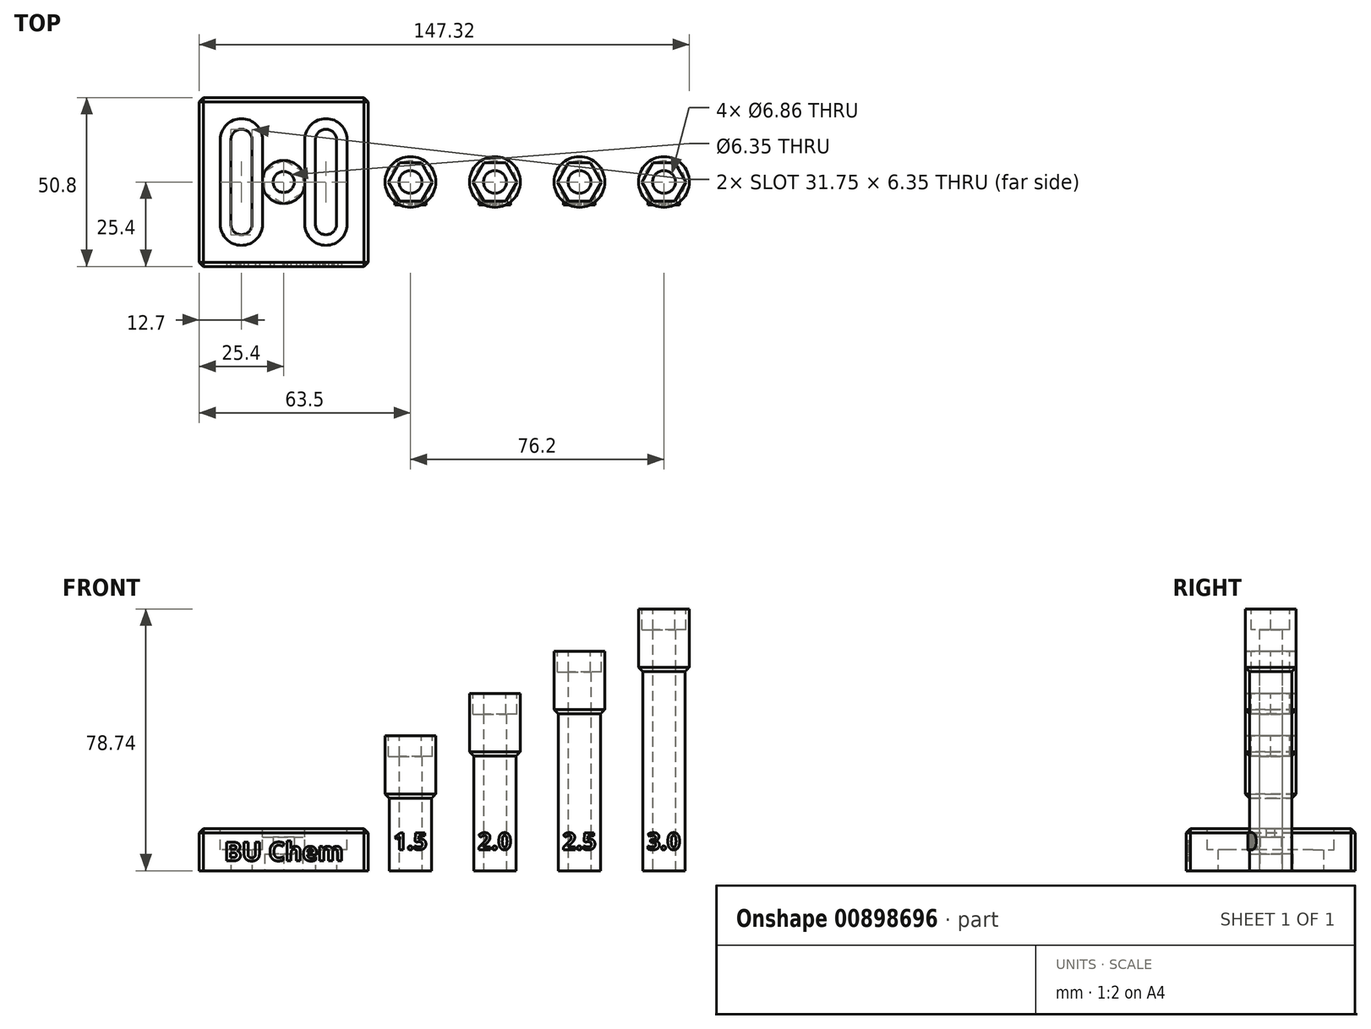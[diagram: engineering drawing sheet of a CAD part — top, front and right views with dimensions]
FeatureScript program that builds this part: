
annotation { "Feature Type Name" : "Feature", "Feature Type Description" : "" }
export const myFeature = defineFeature(function(context is Context, id is Id, definition is map)
    precondition{}
    {
        {
            var Q0;
            Q0=qCreatedBy(makeId("Top.planeOp"),FACE);
            var sketch = newSketch(context, id + "F0", { "sketchPlane" : qUnion([Q0])});
            skLineSegment(sketch, "E0.bottom", {"start": v(-25.4, 25.4) * mm, "end": v(25.4, 25.4) * mm});
            skLineSegment(sketch, "E0.top", {"start": v(-25.4, -25.4) * mm, "end": v(25.4, -25.4) * mm});
            skLineSegment(sketch, "E0.left", {"start": v(-25.4, 25.4) * mm, "end": v(-25.4, -25.4) * mm});
            skLineSegment(sketch, "E0.right", {"start": v(25.4, 25.4) * mm, "end": v(25.4, -25.4) * mm});
            skLineSegment(sketch, "E1", {"start": v(-25.4, 0) * mm, "end": v(129.63, 0) * mm, "construction": true});
            skLineSegment(sketch, "E2", {"start": v(0, -25.4) * mm, "end": v(0, 25.4) * mm, "construction": true});
            skPoint(sketch, "E3", {"position": v(0, 0) * mm});
            skCircle(sketch, "E4", {"center": v(0, 0) * mm, "radius": 3.18 * mm});
            skLineSegment(sketch, "E5", {"start": v(-25.4, -12.7) * mm, "end": v(25.4, -12.7) * mm, "construction": true});
            skLineSegment(sketch, "E6", {"start": v(-12.7, 25.4) * mm, "end": v(-12.7, -25.4) * mm, "construction": true});
            skCircle(sketch, "E7", {"center": v(-12.7, -12.7) * mm, "radius": 3.18 * mm});
            skCircle(sketch, "E8.0.1.0", {"center": v(-12.7, 12.7) * mm, "radius": 3.18 * mm});
            skCircle(sketch, "E8.1.0.0", {"center": v(12.7, -12.7) * mm, "radius": 3.18 * mm});
            skCircle(sketch, "E8.1.1.0", {"center": v(12.7, 12.7) * mm, "radius": 3.18 * mm});
            skLineSegment(sketch, "E8.direction1", {"start": v(-12.7, -12.7) * mm, "end": v(12.7, -12.7) * mm, "construction": true});
            skLineSegment(sketch, "E8.direction2", {"start": v(-12.7, -12.7) * mm, "end": v(-12.7, 12.7) * mm, "construction": true});
            skLineSegment(sketch, "E9", {"start": v(9.52, 12.7) * mm, "end": v(9.52, -12.7) * mm});
            skLineSegment(sketch, "E10", {"start": v(15.87, 12.7) * mm, "end": v(15.87, -12.7) * mm});
            skLineSegment(sketch, "E11", {"start": v(-9.53, 12.7) * mm, "end": v(-9.53, -12.7) * mm});
            skLineSegment(sketch, "E12", {"start": v(-15.88, 12.7) * mm, "end": v(-15.87, -12.7) * mm});
            skCircle(sketch, "E13.cCircle", {"center": v(0, 0) * mm, "radius": 5.72 * mm, "construction": true});
            skLineSegment(sketch, "E13.0", {"start": v(5.72, 3.3) * mm, "end": v(5.72, -3.3) * mm});
            skLineSegment(sketch, "E13.1", {"start": v(5.72, -3.3) * mm, "end": v(0, -6.6) * mm});
            skLineSegment(sketch, "E13.2", {"start": v(0, -6.6) * mm, "end": v(-5.72, -3.3) * mm});
            skLineSegment(sketch, "E13.3", {"start": v(-5.72, -3.3) * mm, "end": v(-5.72, 3.3) * mm});
            skLineSegment(sketch, "E13.4", {"start": v(-5.72, 3.3) * mm, "end": v(0, 6.6) * mm});
            skLineSegment(sketch, "E13.5", {"start": v(0, 6.6) * mm, "end": v(5.72, 3.3) * mm});
            skPoint(sketch, "E13.0.midPoint", {"position": v(5.72, 0) * mm});
            skPoint(sketch, "E14.orphan", {"position": v(25.4, 0) * mm});
            skCircle(sketch, "E15", {"center": v(38.1, 0) * mm, "radius": 6.35 * mm});
            skCircle(sketch, "E16", {"center": v(38.1, 0) * mm, "radius": 3.43 * mm});
            skCircle(sketch, "E17", {"center": v(63.5, 0) * mm, "radius": 3.43 * mm});
            skCircle(sketch, "E18", {"center": v(63.5, 0) * mm, "radius": 6.35 * mm});
            skCircle(sketch, "E19", {"center": v(88.9, 0) * mm, "radius": 3.43 * mm});
            skCircle(sketch, "E20", {"center": v(88.9, 0) * mm, "radius": 6.35 * mm});
            skCircle(sketch, "E21", {"center": v(114.3, 0) * mm, "radius": 3.43 * mm});
            skCircle(sketch, "E22", {"center": v(114.3, 0) * mm, "radius": 6.35 * mm});
            skSolve(sketch);
        }
        {
            var Q0;
            Q0=makeQuery(id+"F0.imprint","IMPRINT",FACE,{"disambiguationData":[TD([[makeQuery(id+"F0.imprint","IMPRINT",EDGE,{"derivedFrom":sQuery(id+"F0.wireOp",EDGE,"E0.bottom")}),-1.0]])]});
            var Q1;
            Q1=makeQuery(id+"F0.imprint","IMPRINT",FACE,{"disambiguationData":[TD([[makeQuery(id+"F0.imprint","IMPRINT",EDGE,{"derivedFrom":sQuery(id+"F0.wireOp",EDGE,"E4")}),-1.0]])]});
            extrude(context, id + "F1", {"entities" : qUnion([Q0, Q1]), "depth" : 12.7 * mm, "offsetDistance" : 25.4 * mm});
        }
        {
            var Q0;
            Q0=makeQuery(id+"F1.opExtrude","CAP_FACE",FACE,{"disambiguationData":[OSD([sQuery(id+"F0.wireOp",EDGE,"E0.bottom"),sQuery(id+"F0.wireOp",EDGE,"E0.top"),sQuery(id+"F0.wireOp",EDGE,"E0.left"),sQuery(id+"F0.wireOp",EDGE,"E0.right"),sQuery(id+"F0.wireOp",EDGE,"E4"),sQuery(id+"F0.wireOp",EDGE,"E7"),sQuery(id+"F0.wireOp",EDGE,"E8.0.1.0"),sQuery(id+"F0.wireOp",EDGE,"E8.1.0.0"),sQuery(id+"F0.wireOp",EDGE,"E8.1.1.0"),sQuery(id+"F0.wireOp",EDGE,"E9"),sQuery(id+"F0.wireOp",EDGE,"E10"),sQuery(id+"F0.wireOp",EDGE,"E11"),sQuery(id+"F0.wireOp",EDGE,"E12")])],"isStart":false});
            var sketch = newSketch(context, id + "F2", { "sketchPlane" : qUnion([Q0])});
            skLineSegment(sketch, "E23.0", {"start": v(-15.88, 12.7) * mm, "end": v(-15.87, -12.7) * mm, "construction": true});
            skCircle(sketch, "E24.0", {"center": v(-12.7, 12.7) * mm, "radius": 3.18 * mm, "construction": true});
            skCircle(sketch, "E25.0", {"center": v(-12.7, -12.7) * mm, "radius": 3.18 * mm, "construction": true});
            skLineSegment(sketch, "E26.0", {"start": v(-9.53, 12.7) * mm, "end": v(-9.53, -12.7) * mm, "construction": true});
            skCircle(sketch, "E27.0", {"center": v(0, 0) * mm, "radius": 3.18 * mm, "construction": true});
            skLineSegment(sketch, "E28.0", {"start": v(9.52, 12.7) * mm, "end": v(9.52, -12.7) * mm, "construction": true});
            skCircle(sketch, "E29.0", {"center": v(12.7, -12.7) * mm, "radius": 3.18 * mm, "construction": true});
            skLineSegment(sketch, "E30.0", {"start": v(15.87, 12.7) * mm, "end": v(15.87, -12.7) * mm, "construction": true});
            skCircle(sketch, "E31.0", {"center": v(12.7, 12.7) * mm, "radius": 3.18 * mm, "construction": true});
            skCircle(sketch, "E32", {"center": v(-12.7, 12.7) * mm, "radius": 6.35 * mm});
            skCircle(sketch, "E33", {"center": v(-12.7, -12.7) * mm, "radius": 6.35 * mm});
            skCircle(sketch, "E34", {"center": v(12.7, 12.7) * mm, "radius": 6.35 * mm});
            skCircle(sketch, "E35", {"center": v(12.7, -12.7) * mm, "radius": 6.35 * mm});
            skCircle(sketch, "E36", {"center": v(0, 0) * mm, "radius": 6.48 * mm});
            skLineSegment(sketch, "E37", {"start": v(-19.05, 12.7) * mm, "end": v(-19.05, -12.7) * mm});
            skLineSegment(sketch, "E38", {"start": v(-6.35, 12.7) * mm, "end": v(-6.35, -12.7) * mm});
            skLineSegment(sketch, "E39", {"start": v(6.35, 12.7) * mm, "end": v(6.35, -12.7) * mm});
            skLineSegment(sketch, "E40", {"start": v(19.05, 12.7) * mm, "end": v(19.05, -12.7) * mm});
            skSolve(sketch);
        }
        {
            var Q0;
            {var subQ0=makeQuery(id+"F1.opExtrude","CAP_EDGE",EDGE,{"disambiguationData":[OSD([sQuery(id+"F0.wireOp",EDGE,"E8.0.1.0")])],"isStart":false});Q0=makeQuery(id+"F2.imprint","IMPRINT",FACE,{"disambiguationData":[TD([[makeQuery(id+"F2.imprint","IMPRINT",EDGE,{"derivedFrom":subQ0}),-1.0]])]});}
            var Q1;
            {var subQ0=sQuery(id+"F2.wireOp",EDGE,"E37");Q1=makeQuery(id+"F2.imprint","IMPRINT",FACE,{"disambiguationData":[TD([[makeQuery(id+"F2.imprint","IMPRINT",EDGE,{"derivedFrom":subQ0}),1.0]])]});}
            var Q2;
            {var subQ0=sQuery(id+"F2.wireOp",EDGE,"E38");var subQ1=sQuery(id+"F2.wireOp",EDGE,"E32");var subQ2=makeQuery(id+"F2.imprint","INTERSECT",VERTEX,{"derivedFrom":[subQ1,subQ0]});Q2=makeQuery(id+"F2.imprint","IMPRINT",FACE,{"disambiguationData":[TD([[makeQuery(id+"F2.imprint","IMPRINT",EDGE,{"disambiguationData":[TD([[subQ2,1.0]])],"derivedFrom":subQ1}),-1.0]])]});}
            var Q3;
            {var subQ0=makeQuery(id+"F1.opExtrude","CAP_EDGE",EDGE,{"disambiguationData":[OSD([sQuery(id+"F0.wireOp",EDGE,"E7")])],"isStart":false});Q3=makeQuery(id+"F2.imprint","IMPRINT",FACE,{"disambiguationData":[TD([[makeQuery(id+"F2.imprint","IMPRINT",EDGE,{"derivedFrom":subQ0}),-1.0]])]});}
            var Q4;
            {var subQ0=makeQuery(id+"F1.opExtrude","CAP_EDGE",EDGE,{"disambiguationData":[OSD([sQuery(id+"F0.wireOp",EDGE,"E8.1.1.0")])],"isStart":false});Q4=makeQuery(id+"F2.imprint","IMPRINT",FACE,{"disambiguationData":[TD([[makeQuery(id+"F2.imprint","IMPRINT",EDGE,{"derivedFrom":subQ0}),-1.0]])]});}
            var Q5;
            {var subQ0=sQuery(id+"F2.wireOp",EDGE,"E39");var subQ1=sQuery(id+"F2.wireOp",EDGE,"E34");var subQ2=makeQuery(id+"F2.imprint","INTERSECT",VERTEX,{"derivedFrom":[subQ1,subQ0]});Q5=makeQuery(id+"F2.imprint","IMPRINT",FACE,{"disambiguationData":[TD([[makeQuery(id+"F2.imprint","IMPRINT",EDGE,{"disambiguationData":[TD([[subQ2,-1.0]])],"derivedFrom":subQ1}),-1.0]])]});}
            var Q6;
            {var subQ0=makeQuery(id+"F1.opExtrude","CAP_EDGE",EDGE,{"disambiguationData":[OSD([sQuery(id+"F0.wireOp",EDGE,"E8.1.0.0")])],"isStart":false});Q6=makeQuery(id+"F2.imprint","IMPRINT",FACE,{"disambiguationData":[TD([[makeQuery(id+"F2.imprint","IMPRINT",EDGE,{"derivedFrom":subQ0}),-1.0]])]});}
            var Q7;
            {var subQ0=sQuery(id+"F2.wireOp",EDGE,"E40");Q7=makeQuery(id+"F2.imprint","IMPRINT",FACE,{"disambiguationData":[TD([[makeQuery(id+"F2.imprint","IMPRINT",EDGE,{"derivedFrom":subQ0}),-1.0]])]});}
            var Q8;
            {var subQ0=sQuery(id+"F2.wireOp",EDGE,"E38");var subQ1=sQuery(id+"F2.wireOp",EDGE,"E36");var subQ2=makeQuery(id+"F2.imprint","INTERSECT",VERTEX,{"disambiguationData":[OD(0.0)],"derivedFrom":[subQ1,subQ0]});Q8=makeQuery(id+"F2.imprint","IMPRINT",FACE,{"disambiguationData":[TD([[makeQuery(id+"F2.imprint","IMPRINT",EDGE,{"disambiguationData":[TD([[subQ2,-1.0]])],"derivedFrom":subQ1}),1.0]])]});}
            var Q9;
            {var subQ0=sQuery(id+"F2.wireOp",EDGE,"E39");var subQ1=sQuery(id+"F2.wireOp",EDGE,"E36");var subQ2=makeQuery(id+"F2.imprint","INTERSECT",VERTEX,{"disambiguationData":[OD(0.0)],"derivedFrom":[subQ1,subQ0]});Q9=makeQuery(id+"F2.imprint","IMPRINT",FACE,{"disambiguationData":[TD([[makeQuery(id+"F2.imprint","IMPRINT",EDGE,{"disambiguationData":[TD([[subQ2,1.0]])],"derivedFrom":subQ1}),1.0]])]});}
            extrude(context, id + "F3", {"entities" : qUnion([Q0, Q1, Q2, Q3, Q4, Q5, Q6, Q7, Q8, Q9]), "operationType" : NewBodyOperationType.REMOVE, "oppositeDirection" : true, "depth" : 6.35 * mm, "offsetDistance" : 25.4 * mm});
        }
        {
            var Q0;
            {var subQ0=sQuery(id+"F2.wireOp",EDGE,"E38");var subQ1=sQuery(id+"F2.wireOp",EDGE,"E36");var subQ2=makeQuery(id+"F2.imprint","INTERSECT",VERTEX,{"disambiguationData":[OD(0.0)],"derivedFrom":[subQ1,subQ0]});Q0=makeQuery(id+"F2.imprint","IMPRINT",FACE,{"disambiguationData":[TD([[makeQuery(id+"F2.imprint","IMPRINT",EDGE,{"disambiguationData":[TD([[subQ2,-1.0]])],"derivedFrom":subQ1}),1.0]])]});}
            var Q1;
            Q1=makeQuery(id+"F2.imprint","IMPRINT",FACE,{"disambiguationData":[TD([[makeQuery(id+"F2.imprint","IMPRINT",EDGE,{"derivedFrom":makeQuery(id+"F1.opExtrude","CAP_EDGE",EDGE,{"disambiguationData":[OSD([sQuery(id+"F0.wireOp",EDGE,"E4")])],"isStart":false})}),-1.0]])]});
            var Q2;
            {var subQ0=sQuery(id+"F2.wireOp",EDGE,"E39");var subQ1=sQuery(id+"F2.wireOp",EDGE,"E36");var subQ2=makeQuery(id+"F2.imprint","INTERSECT",VERTEX,{"disambiguationData":[OD(0.0)],"derivedFrom":[subQ1,subQ0]});Q2=makeQuery(id+"F2.imprint","IMPRINT",FACE,{"disambiguationData":[TD([[makeQuery(id+"F2.imprint","IMPRINT",EDGE,{"disambiguationData":[TD([[subQ2,1.0]])],"derivedFrom":subQ1}),1.0]])]});}
            extrude(context, id + "F4", {"entities" : qUnion([Q0, Q1, Q2]), "operationType" : NewBodyOperationType.REMOVE, "oppositeDirection" : true, "depth" : 2.54 * mm, "offsetDistance" : 25.4 * mm});
        }
        {
            var Q0;
            Q0=makeQuery(id+"F1.opExtrude","CAP_EDGE",EDGE,{"disambiguationData":[OSD([sQuery(id+"F0.wireOp",EDGE,"E0.top")])],"isStart":false});
            var Q1;
            Q1=makeQuery(id+"F1.opExtrude","CAP_EDGE",EDGE,{"disambiguationData":[OSD([sQuery(id+"F0.wireOp",EDGE,"E0.left")])],"isStart":false});
            var Q2;
            Q2=makeQuery(id+"F1.opExtrude","CAP_EDGE",EDGE,{"disambiguationData":[OSD([sQuery(id+"F0.wireOp",EDGE,"E0.bottom")])],"isStart":false});
            var Q3;
            Q3=makeQuery(id+"F1.opExtrude","CAP_EDGE",EDGE,{"disambiguationData":[OSD([sQuery(id+"F0.wireOp",EDGE,"E0.right")])],"isStart":false});
            var Q4;
            Q4=makeQuery(id+"F1.opExtrude","SWEPT_EDGE",EDGE,{"disambiguationData":[OSD([sQuery(id+"F0.wireOp",EDGE,"E0.top"),sQuery(id+"F0.wireOp",EDGE,"E0.left")])]});
            var Q5;
            Q5=makeQuery(id+"F1.opExtrude","SWEPT_EDGE",EDGE,{"disambiguationData":[OSD([sQuery(id+"F0.wireOp",EDGE,"E0.top"),sQuery(id+"F0.wireOp",EDGE,"E0.right")])]});
            var Q6;
            Q6=makeQuery(id+"F1.opExtrude","SWEPT_EDGE",EDGE,{"disambiguationData":[OSD([sQuery(id+"F0.wireOp",EDGE,"E0.bottom"),sQuery(id+"F0.wireOp",EDGE,"E0.left")])]});
            var Q7;
            Q7=makeQuery(id+"F1.opExtrude","SWEPT_EDGE",EDGE,{"disambiguationData":[OSD([sQuery(id+"F0.wireOp",EDGE,"E0.bottom"),sQuery(id+"F0.wireOp",EDGE,"E0.right")])]});
            chamfer(context, id + "F5", {"entities" : qUnion([Q0, Q1, Q2, Q3, Q4, Q5, Q6, Q7]), "width" : 1.27 * mm, "tangentPropagation" : true});
        }
        {
            var Q0;
            Q0=makeQuery(id+"F0.imprint","IMPRINT",FACE,{"disambiguationData":[TD([[makeQuery(id+"F0.imprint","IMPRINT",EDGE,{"derivedFrom":sQuery(id+"F0.wireOp",EDGE,"E4")}),-1.0]])]});
            extrude(context, id + "F6", {"entities" : qUnion([Q0]), "operationType" : NewBodyOperationType.REMOVE, "depth" : 5.08 * mm, "offsetDistance" : 25.4 * mm});
        }
        {
            var Q0;
            Q0=makeQuery(id+"F1.opExtrude","SWEPT_FACE",FACE,{"disambiguationData":[OSD([sQuery(id+"F0.wireOp",EDGE,"E0.top")])]});
            var sketch = newSketch(context, id + "F7", { "sketchPlane" : qUnion([Q0])});
            skText(sketch, "E41", { "text": "BU Chem", "fontName": "OpenSans-Bold.ttf"});
            skLineSegment(sketch, "E42", {"start": v(0, 11.43) * mm, "end": v(0, 0) * mm, "construction": true});
            const initialGuessF7  = {"E41": [-0.01786, 0.00298, 1, 0, 0.00566]};
            skSetInitialGuess(sketch, initialGuessF7);
            skSolve(sketch);
        }
        {
            var Q0;
            Q0=makeQuery(id+"F7.imprint","IMPRINT",FACE,{"disambiguationData":[TD([[makeQuery(id+"F7.imprint","IMPRINT",EDGE,{"derivedFrom":sQuery(id+"F7.wireOp",EDGE,"E41.sketch_text.stroke-25")}),-1.0]])]});
            var Q1;
            Q1=makeQuery(id+"F7.imprint","IMPRINT",FACE,{"disambiguationData":[TD([[makeQuery(id+"F7.imprint","IMPRINT",EDGE,{"derivedFrom":sQuery(id+"F7.wireOp",EDGE,"E41.sketch_text.stroke-0")}),-1.0]])]});
            var Q2;
            Q2=makeQuery(id+"F7.imprint","IMPRINT",FACE,{"disambiguationData":[TD([[makeQuery(id+"F7.imprint","IMPRINT",EDGE,{"derivedFrom":sQuery(id+"F7.wireOp",EDGE,"E41.sketch_text.stroke-40")}),-1.0]])]});
            var Q3;
            Q3=makeQuery(id+"F7.imprint","IMPRINT",FACE,{"disambiguationData":[TD([[makeQuery(id+"F7.imprint","IMPRINT",EDGE,{"derivedFrom":sQuery(id+"F7.wireOp",EDGE,"E41.sketch_text.stroke-55")}),-1.0]])]});
            var Q4;
            Q4=makeQuery(id+"F7.imprint","IMPRINT",FACE,{"disambiguationData":[TD([[makeQuery(id+"F7.imprint","IMPRINT",EDGE,{"derivedFrom":sQuery(id+"F7.wireOp",EDGE,"E41.sketch_text.stroke-72")}),-1.0]])]});
            var Q5;
            Q5=makeQuery(id+"F7.imprint","IMPRINT",FACE,{"disambiguationData":[TD([[makeQuery(id+"F7.imprint","IMPRINT",EDGE,{"derivedFrom":sQuery(id+"F7.wireOp",EDGE,"E41.sketch_text.stroke-92")}),-1.0]])]});
            extrude(context, id + "F8", {"entities" : qUnion([Q0, Q1, Q2, Q3, Q4, Q5]), "operationType" : NewBodyOperationType.REMOVE, "oppositeDirection" : true, "depth" : 1.27 * mm, "offsetDistance" : 25.4 * mm});
        }
        {
            var Q0;
            Q0=makeQuery(id+"F0.imprint","IMPRINT",FACE,{"disambiguationData":[TD([[makeQuery(id+"F0.imprint","IMPRINT",EDGE,{"derivedFrom":sQuery(id+"F0.wireOp",EDGE,"E19")}),-1.0]])]});
            extrude(context, id + "F9", {"entities" : qUnion([Q0]), "depth" : 47.24 * mm, "offsetDistance" : 25.4 * mm});
        }
        {
            var Q0;
            Q0=makeQuery(id+"F0.imprint","IMPRINT",FACE,{"disambiguationData":[TD([[makeQuery(id+"F0.imprint","IMPRINT",EDGE,{"derivedFrom":sQuery(id+"F0.wireOp",EDGE,"E15")}),1.0]])]});
            extrude(context, id + "F10", {"entities" : qUnion([Q0]), "depth" : 21.84 * mm, "offsetDistance" : 25.4 * mm});
        }
        {
            var Q0;
            Q0=makeQuery(id+"F0.imprint","IMPRINT",FACE,{"disambiguationData":[TD([[makeQuery(id+"F0.imprint","IMPRINT",EDGE,{"derivedFrom":sQuery(id+"F0.wireOp",EDGE,"E17")}),-1.0]])]});
            extrude(context, id + "F11", {"entities" : qUnion([Q0]), "depth" : 34.54 * mm, "offsetDistance" : 25.4 * mm});
        }
        {
            var Q0;
            Q0=makeQuery(id+"F0.imprint","IMPRINT",FACE,{"disambiguationData":[TD([[makeQuery(id+"F0.imprint","IMPRINT",EDGE,{"derivedFrom":sQuery(id+"F0.wireOp",EDGE,"E21")}),-1.0]])]});
            extrude(context, id + "F12", {"entities" : qUnion([Q0]), "depth" : 59.94 * mm, "offsetDistance" : 25.4 * mm});
        }
        {
            var Q0;
            Q0=makeQuery(id+"F10.opExtrude","CAP_FACE",FACE,{"disambiguationData":[OSD([sQuery(id+"F0.wireOp",EDGE,"E15"),sQuery(id+"F0.wireOp",EDGE,"E16")])],"isStart":false});
            var sketch = newSketch(context, id + "F13", { "sketchPlane" : qUnion([Q0])});
            skCircle(sketch, "E43.0", {"center": v(38.1, 0) * mm, "radius": 3.43 * mm});
            skCircle(sketch, "E44", {"center": v(38.1, 0) * mm, "radius": 7.62 * mm});
            skSolve(sketch);
        }
        {
            var Q0;
            Q0=makeQuery(id+"F13.imprint","IMPRINT",FACE,{"disambiguationData":[TD([[makeQuery(id+"F13.imprint","IMPRINT",EDGE,{"derivedFrom":sQuery(id+"F13.wireOp",EDGE,"E43.0")}),-1.0]])]});
            var Q1;
            Q1=makeQuery(id+"F13.imprint","IMPRINT",FACE,{"disambiguationData":[TD([[makeQuery(id+"F13.imprint","IMPRINT",EDGE,{"derivedFrom":sQuery(id+"F13.wireOp",EDGE,"E44")}),1.0]])]});
            extrude(context, id + "F14", {"entities" : qUnion([Q0, Q1]), "operationType" : NewBodyOperationType.ADD, "depth" : 18.8 * mm, "offsetDistance" : 25.4 * mm});
        }
        {
            var Q0;
            Q0=makeQuery(id+"F11.opExtrude","CAP_FACE",FACE,{"disambiguationData":[OSD([sQuery(id+"F0.wireOp",EDGE,"E17"),sQuery(id+"F0.wireOp",EDGE,"E18")])],"isStart":false});
            var sketch = newSketch(context, id + "F15", { "sketchPlane" : qUnion([Q0])});
            skCircle(sketch, "E45.0", {"center": v(63.5, 0) * mm, "radius": 3.43 * mm});
            skCircle(sketch, "E46", {"center": v(63.5, 0) * mm, "radius": 7.62 * mm});
            skSolve(sketch);
        }
        {
            var Q0;
            Q0=makeQuery(id+"F15.imprint","IMPRINT",FACE,{"disambiguationData":[TD([[makeQuery(id+"F15.imprint","IMPRINT",EDGE,{"derivedFrom":sQuery(id+"F15.wireOp",EDGE,"E45.0")}),-1.0]])]});
            var Q1;
            Q1=makeQuery(id+"F15.imprint","IMPRINT",FACE,{"disambiguationData":[TD([[makeQuery(id+"F15.imprint","IMPRINT",EDGE,{"derivedFrom":sQuery(id+"F15.wireOp",EDGE,"E46")}),1.0]])]});
            extrude(context, id + "F16", {"entities" : qUnion([Q0, Q1]), "operationType" : NewBodyOperationType.ADD, "depth" : 18.8 * mm, "offsetDistance" : 25.4 * mm});
        }
        {
            var Q0;
            Q0=makeQuery(id+"F9.opExtrude","CAP_FACE",FACE,{"disambiguationData":[OSD([sQuery(id+"F0.wireOp",EDGE,"E19"),sQuery(id+"F0.wireOp",EDGE,"E20")])],"isStart":false});
            var sketch = newSketch(context, id + "F17", { "sketchPlane" : qUnion([Q0])});
            skCircle(sketch, "E47.0", {"center": v(88.9, 0) * mm, "radius": 3.43 * mm});
            skCircle(sketch, "E48", {"center": v(88.9, 0) * mm, "radius": 7.62 * mm});
            skSolve(sketch);
        }
        {
            var Q0;
            Q0=makeQuery(id+"F17.imprint","IMPRINT",FACE,{"disambiguationData":[TD([[makeQuery(id+"F17.imprint","IMPRINT",EDGE,{"derivedFrom":sQuery(id+"F17.wireOp",EDGE,"E47.0")}),-1.0]])]});
            var Q1;
            Q1=makeQuery(id+"F17.imprint","IMPRINT",FACE,{"disambiguationData":[TD([[makeQuery(id+"F17.imprint","IMPRINT",EDGE,{"derivedFrom":sQuery(id+"F17.wireOp",EDGE,"E48")}),1.0]])]});
            extrude(context, id + "F18", {"entities" : qUnion([Q0, Q1]), "operationType" : NewBodyOperationType.ADD, "depth" : 18.8 * mm, "offsetDistance" : 25.4 * mm});
        }
        {
            var Q0;
            Q0=makeQuery(id+"F12.opExtrude","CAP_FACE",FACE,{"disambiguationData":[OSD([sQuery(id+"F0.wireOp",EDGE,"E21"),sQuery(id+"F0.wireOp",EDGE,"E22")])],"isStart":false});
            var sketch = newSketch(context, id + "F19", { "sketchPlane" : qUnion([Q0])});
            skCircle(sketch, "E49.0", {"center": v(114.3, 0) * mm, "radius": 3.43 * mm});
            skCircle(sketch, "E50", {"center": v(114.3, 0) * mm, "radius": 7.62 * mm});
            skSolve(sketch);
        }
        {
            var Q0;
            Q0=makeQuery(id+"F19.imprint","IMPRINT",FACE,{"disambiguationData":[TD([[makeQuery(id+"F19.imprint","IMPRINT",EDGE,{"derivedFrom":sQuery(id+"F19.wireOp",EDGE,"E49.0")}),-1.0]])]});
            var Q1;
            Q1=makeQuery(id+"F19.imprint","IMPRINT",FACE,{"disambiguationData":[TD([[makeQuery(id+"F19.imprint","IMPRINT",EDGE,{"derivedFrom":sQuery(id+"F19.wireOp",EDGE,"E50")}),1.0]])]});
            extrude(context, id + "F20", {"entities" : qUnion([Q0, Q1]), "operationType" : NewBodyOperationType.ADD, "depth" : 18.8 * mm, "offsetDistance" : 25.4 * mm});
        }
        {
            var Q0;
            Q0=makeQuery(id+"F14.opExtrude","CAP_EDGE",EDGE,{"disambiguationData":[OSD([sQuery(id+"F13.wireOp",EDGE,"E44")])],"isStart":true});
            var Q1;
            Q1=makeQuery(id+"F16.opExtrude","CAP_EDGE",EDGE,{"disambiguationData":[OSD([sQuery(id+"F15.wireOp",EDGE,"E46")])],"isStart":true});
            var Q2;
            Q2=makeQuery(id+"F18.opExtrude","CAP_EDGE",EDGE,{"disambiguationData":[OSD([sQuery(id+"F17.wireOp",EDGE,"E48")])],"isStart":true});
            var Q3;
            Q3=makeQuery(id+"F20.opExtrude","CAP_EDGE",EDGE,{"disambiguationData":[OSD([sQuery(id+"F19.wireOp",EDGE,"E50")])],"isStart":true});
            chamfer(context, id + "F21", {"entities" : qUnion([Q0, Q1, Q2, Q3]), "width" : 1.27 * mm, "tangentPropagation" : true});
        }
        {
            var Q0;
            Q0=makeQuery(id+"F14.opExtrude","CAP_FACE",FACE,{"disambiguationData":[OSD([sQuery(id+"F13.wireOp",EDGE,"E43.0"),sQuery(id+"F13.wireOp",EDGE,"E44")])],"isStart":false});
            var sketch = newSketch(context, id + "F22", { "sketchPlane" : qUnion([Q0])});
            skCircle(sketch, "E51.cCircle", {"center": v(38.1, 0) * mm, "radius": 6.65 * mm, "construction": true});
            skLineSegment(sketch, "E51.0", {"start": v(44.75, 0) * mm, "end": v(41.43, -5.76) * mm});
            skLineSegment(sketch, "E51.1", {"start": v(41.43, -5.76) * mm, "end": v(34.77, -5.76) * mm});
            skLineSegment(sketch, "E51.2", {"start": v(34.77, -5.76) * mm, "end": v(31.45, 0) * mm});
            skLineSegment(sketch, "E51.3", {"start": v(31.45, 0) * mm, "end": v(34.77, 5.76) * mm});
            skLineSegment(sketch, "E51.4", {"start": v(34.77, 5.76) * mm, "end": v(41.43, 5.76) * mm});
            skLineSegment(sketch, "E51.5", {"start": v(41.43, 5.76) * mm, "end": v(44.75, 0) * mm});
            skSolve(sketch);
        }
        {
            var Q0;
            Q0=makeQuery(id+"F22.imprint","IMPRINT",FACE,{"disambiguationData":[TD([[makeQuery(id+"F22.imprint","IMPRINT",EDGE,{"derivedFrom":sQuery(id+"F22.wireOp",EDGE,"E51.0")}),-1.0]])]});
            extrude(context, id + "F23", {"entities" : qUnion([Q0]), "operationType" : NewBodyOperationType.REMOVE, "oppositeDirection" : true, "depth" : 6.22 * mm, "offsetDistance" : 25.4 * mm});
        }
        {
            var Q0;
            Q0=makeQuery(id+"F16.opExtrude","CAP_FACE",FACE,{"disambiguationData":[OSD([sQuery(id+"F15.wireOp",EDGE,"E45.0"),sQuery(id+"F15.wireOp",EDGE,"E46")])],"isStart":false});
            var sketch = newSketch(context, id + "F24", { "sketchPlane" : qUnion([Q0])});
            skCircle(sketch, "E52.cCircle", {"center": v(63.5, 0) * mm, "radius": 6.65 * mm, "construction": true});
            skLineSegment(sketch, "E52.0", {"start": v(70.15, 0) * mm, "end": v(66.83, -5.76) * mm});
            skLineSegment(sketch, "E52.1", {"start": v(66.83, -5.76) * mm, "end": v(60.17, -5.76) * mm});
            skLineSegment(sketch, "E52.2", {"start": v(60.17, -5.76) * mm, "end": v(56.85, 0) * mm});
            skLineSegment(sketch, "E52.3", {"start": v(56.85, 0) * mm, "end": v(60.17, 5.76) * mm});
            skLineSegment(sketch, "E52.4", {"start": v(60.17, 5.76) * mm, "end": v(66.83, 5.76) * mm});
            skLineSegment(sketch, "E52.5", {"start": v(66.83, 5.76) * mm, "end": v(70.15, 0) * mm});
            skSolve(sketch);
        }
        {
            var Q0;
            Q0=makeQuery(id+"F24.imprint","IMPRINT",FACE,{"disambiguationData":[TD([[makeQuery(id+"F24.imprint","IMPRINT",EDGE,{"derivedFrom":sQuery(id+"F24.wireOp",EDGE,"E52.0")}),-1.0]])]});
            extrude(context, id + "F25", {"entities" : qUnion([Q0]), "operationType" : NewBodyOperationType.REMOVE, "oppositeDirection" : true, "depth" : 6.22 * mm, "offsetDistance" : 25.4 * mm});
        }
        {
            var Q0;
            Q0=makeQuery(id+"F18.opExtrude","CAP_FACE",FACE,{"disambiguationData":[OSD([sQuery(id+"F17.wireOp",EDGE,"E47.0"),sQuery(id+"F17.wireOp",EDGE,"E48")])],"isStart":false});
            var sketch = newSketch(context, id + "F26", { "sketchPlane" : qUnion([Q0])});
            skCircle(sketch, "E53.cCircle", {"center": v(88.9, 0) * mm, "radius": 6.65 * mm, "construction": true});
            skLineSegment(sketch, "E53.0", {"start": v(95.55, 0) * mm, "end": v(92.23, -5.76) * mm});
            skLineSegment(sketch, "E53.1", {"start": v(92.23, -5.76) * mm, "end": v(85.57, -5.76) * mm});
            skLineSegment(sketch, "E53.2", {"start": v(85.57, -5.76) * mm, "end": v(82.25, 0) * mm});
            skLineSegment(sketch, "E53.3", {"start": v(82.25, 0) * mm, "end": v(85.57, 5.76) * mm});
            skLineSegment(sketch, "E53.4", {"start": v(85.57, 5.76) * mm, "end": v(92.23, 5.76) * mm});
            skLineSegment(sketch, "E53.5", {"start": v(92.23, 5.76) * mm, "end": v(95.55, 0) * mm});
            skSolve(sketch);
        }
        {
            var Q0;
            Q0=makeQuery(id+"F26.imprint","IMPRINT",FACE,{"disambiguationData":[TD([[makeQuery(id+"F26.imprint","IMPRINT",EDGE,{"derivedFrom":sQuery(id+"F26.wireOp",EDGE,"E53.0")}),-1.0]])]});
            extrude(context, id + "F27", {"entities" : qUnion([Q0]), "operationType" : NewBodyOperationType.REMOVE, "oppositeDirection" : true, "depth" : 6.22 * mm, "offsetDistance" : 25.4 * mm});
        }
        {
            var Q0;
            Q0=makeQuery(id+"F20.opExtrude","CAP_FACE",FACE,{"disambiguationData":[OSD([sQuery(id+"F19.wireOp",EDGE,"E49.0"),sQuery(id+"F19.wireOp",EDGE,"E50")])],"isStart":false});
            var sketch = newSketch(context, id + "F28", { "sketchPlane" : qUnion([Q0])});
            skCircle(sketch, "E54.cCircle", {"center": v(114.3, 0) * mm, "radius": 6.65 * mm, "construction": true});
            skLineSegment(sketch, "E54.0", {"start": v(120.95, 0) * mm, "end": v(117.63, -5.76) * mm});
            skLineSegment(sketch, "E54.1", {"start": v(117.63, -5.76) * mm, "end": v(110.97, -5.76) * mm});
            skLineSegment(sketch, "E54.2", {"start": v(110.97, -5.76) * mm, "end": v(107.65, 0) * mm});
            skLineSegment(sketch, "E54.3", {"start": v(107.65, 0) * mm, "end": v(110.97, 5.76) * mm});
            skLineSegment(sketch, "E54.4", {"start": v(110.97, 5.76) * mm, "end": v(117.63, 5.76) * mm});
            skLineSegment(sketch, "E54.5", {"start": v(117.63, 5.76) * mm, "end": v(120.95, 0) * mm});
            skSolve(sketch);
        }
        {
            var Q0;
            Q0=makeQuery(id+"F28.imprint","IMPRINT",FACE,{"disambiguationData":[TD([[makeQuery(id+"F28.imprint","IMPRINT",EDGE,{"derivedFrom":sQuery(id+"F28.wireOp",EDGE,"E54.0")}),-1.0]])]});
            extrude(context, id + "F29", {"entities" : qUnion([Q0]), "operationType" : NewBodyOperationType.REMOVE, "oppositeDirection" : true, "depth" : 6.22 * mm, "offsetDistance" : 25.4 * mm});
        }
        {
            var Q0;
            Q0=qCreatedBy(makeId("Front.planeOp"),FACE);
            cPlane(context, id + "F30", {"entities" : qUnion([Q0]), "cplaneType" : CPlaneType.OFFSET, "offset" : 6.86 * mm, "width" : 152.4 * mm, "height" : 152.4 * mm});
        }
        {
            var Q0;
            Q0=qCreatedBy(id+"F30.planeOp",FACE);
            var sketch = newSketch(context, id + "F31", { "sketchPlane" : qUnion([Q0])});
            skLineSegment(sketch, "E55", {"start": v(24.53, 6.35) * mm, "end": v(120.33, 6.35) * mm, "construction": true});
            skLineSegment(sketch, "E56.0", {"start": v(-25.4, 0) * mm, "end": v(129.63, 0) * mm, "construction": true});
            skLineSegment(sketch, "E57", {"start": v(38.1, 0) * mm, "end": v(38.1, 16.17) * mm, "construction": true});
            skLineSegment(sketch, "E58.1.0.0", {"start": v(63.5, 0) * mm, "end": v(63.5, 16.17) * mm, "construction": true});
            skLineSegment(sketch, "E58.2.0.0", {"start": v(88.9, 0) * mm, "end": v(88.9, 16.17) * mm, "construction": true});
            skLineSegment(sketch, "E58.3.0.0", {"start": v(114.3, 0) * mm, "end": v(114.3, 16.17) * mm, "construction": true});
            skLineSegment(sketch, "E58.direction1", {"start": v(38.1, 0) * mm, "end": v(63.5, 0) * mm, "construction": true});
            skLineSegment(sketch, "E59", {"start": v(24.53, 11.43) * mm, "end": v(120.33, 11.43) * mm, "construction": true});
            skText(sketch, "E60", { "text": "1.5", "fontName": "OpenSans-Bold.ttf"});
            skText(sketch, "E61", { "text": "2.0", "fontName": "OpenSans-Bold.ttf"});
            skText(sketch, "E62", { "text": "2.5", "fontName": "OpenSans-Bold.ttf"});
            skText(sketch, "E63", { "text": "3.0", "fontName": "OpenSans-Bold.ttf"});
            const initialGuessF31  = {"E60": [0.033, 0.00635, 1, 0, 0.00508], "E61": [0.05836, 0.00635, 1, 0, 0.00508], "E62": [0.0838, 0.00635, 1, 0, 0.00508], "E63": [0.10916, 0.00635, 1, 0, 0.00508]};
            skSetInitialGuess(sketch, initialGuessF31);
            skSolve(sketch);
        }
        {
            var Q0;
            Q0=makeQuery(id+"F31.imprint","IMPRINT",FACE,{"disambiguationData":[TD([[makeQuery(id+"F31.imprint","IMPRINT",EDGE,{"derivedFrom":sQuery(id+"F31.wireOp",EDGE,"E60.sketch_text.stroke-0")}),-1.0]])]});
            var Q1;
            Q1=makeQuery(id+"F31.imprint","IMPRINT",FACE,{"disambiguationData":[TD([[makeQuery(id+"F31.imprint","IMPRINT",EDGE,{"derivedFrom":sQuery(id+"F31.wireOp",EDGE,"E60.sketch_text.stroke-10")}),-1.0]])]});
            var Q2;
            Q2=makeQuery(id+"F31.imprint","IMPRINT",FACE,{"disambiguationData":[TD([[makeQuery(id+"F31.imprint","IMPRINT",EDGE,{"derivedFrom":sQuery(id+"F31.wireOp",EDGE,"E60.sketch_text.stroke-18")}),-1.0]])]});
            extrude(context, id + "F32", {"entities" : qUnion([Q0, Q1, Q2]), "operationType" : NewBodyOperationType.ADD, "oppositeDirection" : true, "depth" : 3.17 * mm, "offsetDistance" : 25.4 * mm});
        }
        {
            var Q0;
            Q0=makeQuery(id+"F31.imprint","IMPRINT",FACE,{"disambiguationData":[TD([[makeQuery(id+"F31.imprint","IMPRINT",EDGE,{"derivedFrom":sQuery(id+"F31.wireOp",EDGE,"E61.sketch_text.stroke-0")}),-1.0]])]});
            var Q1;
            Q1=makeQuery(id+"F31.imprint","IMPRINT",FACE,{"disambiguationData":[TD([[makeQuery(id+"F31.imprint","IMPRINT",EDGE,{"derivedFrom":sQuery(id+"F31.wireOp",EDGE,"E61.sketch_text.stroke-24")}),-1.0]])]});
            var Q2;
            Q2=makeQuery(id+"F31.imprint","IMPRINT",FACE,{"disambiguationData":[TD([[makeQuery(id+"F31.imprint","IMPRINT",EDGE,{"derivedFrom":sQuery(id+"F31.wireOp",EDGE,"E61.sketch_text.stroke-32")}),-1.0]])]});
            extrude(context, id + "F33", {"entities" : qUnion([Q0, Q1, Q2]), "operationType" : NewBodyOperationType.ADD, "oppositeDirection" : true, "depth" : 3.17 * mm, "offsetDistance" : 25.4 * mm});
        }
        {
            var Q0;
            Q0=makeQuery(id+"F31.imprint","IMPRINT",FACE,{"disambiguationData":[TD([[makeQuery(id+"F31.imprint","IMPRINT",EDGE,{"derivedFrom":sQuery(id+"F31.wireOp",EDGE,"E62.sketch_text.stroke-0")}),-1.0]])]});
            var Q1;
            Q1=makeQuery(id+"F31.imprint","IMPRINT",FACE,{"disambiguationData":[TD([[makeQuery(id+"F31.imprint","IMPRINT",EDGE,{"derivedFrom":sQuery(id+"F31.wireOp",EDGE,"E62.sketch_text.stroke-24")}),-1.0]])]});
            var Q2;
            Q2=makeQuery(id+"F31.imprint","IMPRINT",FACE,{"disambiguationData":[TD([[makeQuery(id+"F31.imprint","IMPRINT",EDGE,{"derivedFrom":sQuery(id+"F31.wireOp",EDGE,"E62.sketch_text.stroke-32")}),-1.0]])]});
            extrude(context, id + "F34", {"entities" : qUnion([Q0, Q1, Q2]), "operationType" : NewBodyOperationType.ADD, "oppositeDirection" : true, "depth" : 3.17 * mm, "offsetDistance" : 25.4 * mm});
        }
        {
            var Q0;
            Q0=makeQuery(id+"F31.imprint","IMPRINT",FACE,{"disambiguationData":[TD([[makeQuery(id+"F31.imprint","IMPRINT",EDGE,{"derivedFrom":sQuery(id+"F31.wireOp",EDGE,"E63.sketch_text.stroke-0")}),-1.0]])]});
            var Q1;
            Q1=makeQuery(id+"F31.imprint","IMPRINT",FACE,{"disambiguationData":[TD([[makeQuery(id+"F31.imprint","IMPRINT",EDGE,{"derivedFrom":sQuery(id+"F31.wireOp",EDGE,"E63.sketch_text.stroke-27")}),-1.0]])]});
            var Q2;
            Q2=makeQuery(id+"F31.imprint","IMPRINT",FACE,{"disambiguationData":[TD([[makeQuery(id+"F31.imprint","IMPRINT",EDGE,{"derivedFrom":sQuery(id+"F31.wireOp",EDGE,"E63.sketch_text.stroke-35")}),-1.0]])]});
            extrude(context, id + "F35", {"entities" : qUnion([Q0, Q1, Q2]), "operationType" : NewBodyOperationType.ADD, "oppositeDirection" : true, "depth" : 3.17 * mm, "offsetDistance" : 25.4 * mm});
        }
    });
